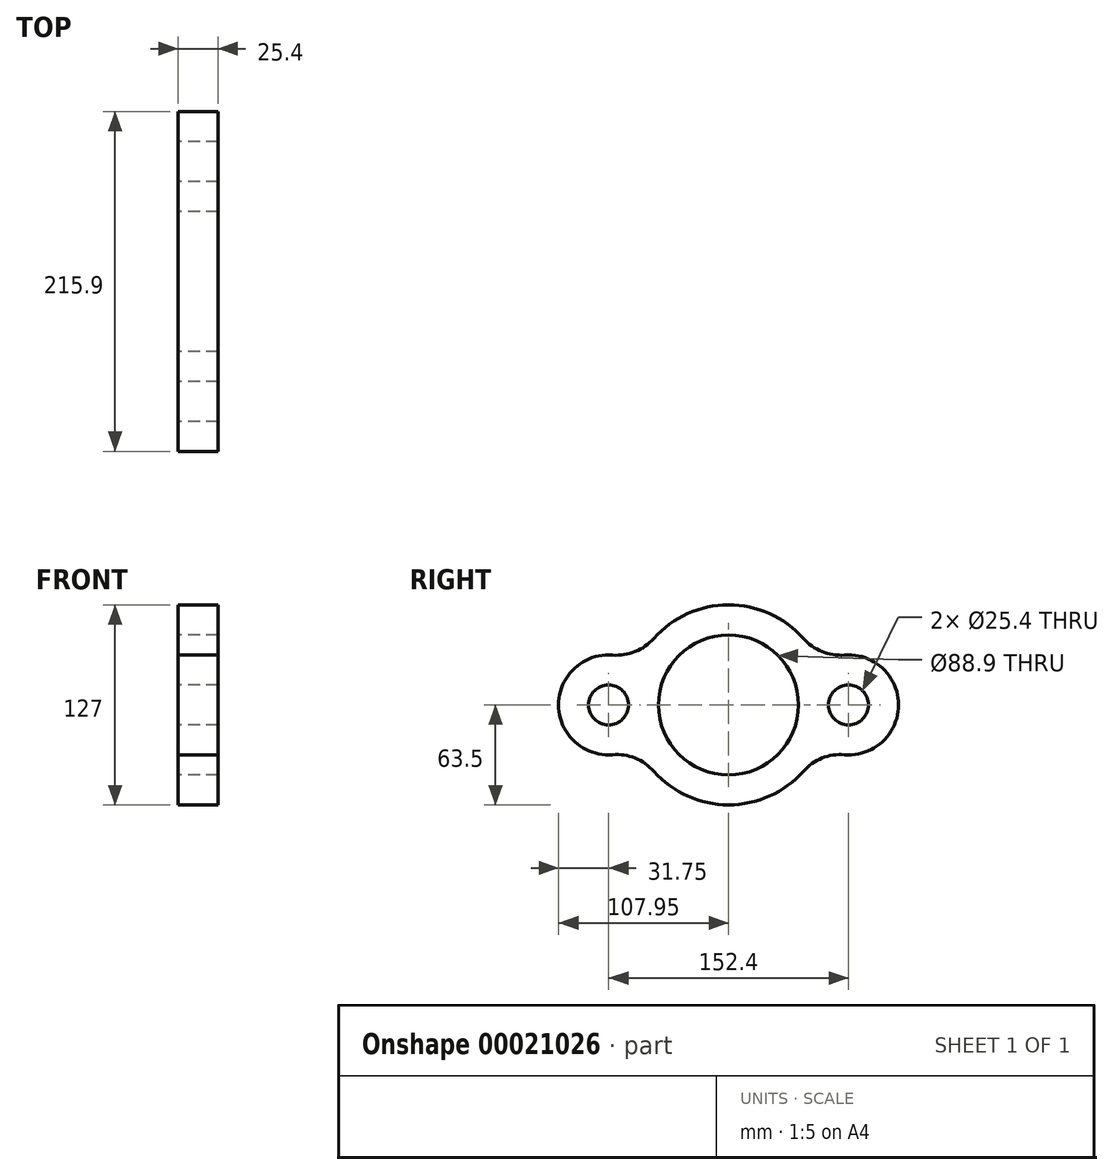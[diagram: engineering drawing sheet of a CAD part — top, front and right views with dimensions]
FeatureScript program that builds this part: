
annotation { "Feature Type Name" : "Feature", "Feature Type Description" : "" }
export const myFeature = defineFeature(function(context is Context, id is Id, definition is map)
    precondition{}
    {
        {
            var Q0;
            Q0=qCreatedBy(makeId("Right.planeOp"),FACE);
            var sketch = newSketch(context, id + "F0", { "sketchPlane" : qUnion([Q0])});
            skCircle(sketch, "E0", {"center": v(0, 0) * mm, "radius": 44.45 * mm});
            skCircle(sketch, "E1", {"center": v(76.2, 0) * mm, "radius": 12.7 * mm});
            skCircle(sketch, "E2", {"center": v(-76.2, 0) * mm, "radius": 12.7 * mm});
            skArc(sketch, "E3", {"start": v(-73.69, 31.65) * mm, "mid": v(-107.95, 0) * mm, "end": v(-73.69, -31.65) * mm});
            skArc(sketch, "E4", {"start": v(73.69, -31.65) * mm, "mid": v(107.95, 0) * mm, "end": v(73.69, 31.65) * mm});
            skArc(sketch, "E5", {"start": v(-47.45, -42.2) * mm, "mid": v(0, -63.5) * mm, "end": v(47.45, -42.2) * mm});
            skArc(sketch, "E6", {"start": v(-73.69, 31.65) * mm, "mid": v(-59.33, 33.84) * mm, "end": v(-47.45, 42.2) * mm});
            skArc(sketch, "E7", {"start": v(47.45, 42.2) * mm, "mid": v(59.33, 33.84) * mm, "end": v(73.69, 31.65) * mm});
            skArc(sketch, "E8", {"start": v(73.69, -31.65) * mm, "mid": v(59.33, -33.84) * mm, "end": v(47.45, -42.2) * mm});
            skArc(sketch, "E9", {"start": v(-47.45, -42.2) * mm, "mid": v(-59.33, -33.84) * mm, "end": v(-73.69, -31.65) * mm});
            skArc(sketch, "E10.trimOffspring", {"start": v(47.45, 42.2) * mm, "mid": v(0, 63.5) * mm, "end": v(-47.45, 42.2) * mm});
            skSolve(sketch);
        }
        {
            var Q0;
            Q0=makeQuery(id+"F0.imprint","IMPRINT",FACE,{"disambiguationData":[TD([[makeQuery(id+"F0.imprint","IMPRINT",EDGE,{"derivedFrom":sQuery(id+"F0.wireOp",EDGE,"E0")}),-1.0]])]});
            extrude(context, id + "F1", {"entities" : qUnion([Q0]), "depth" : 25.4 * mm});
        }
    });
